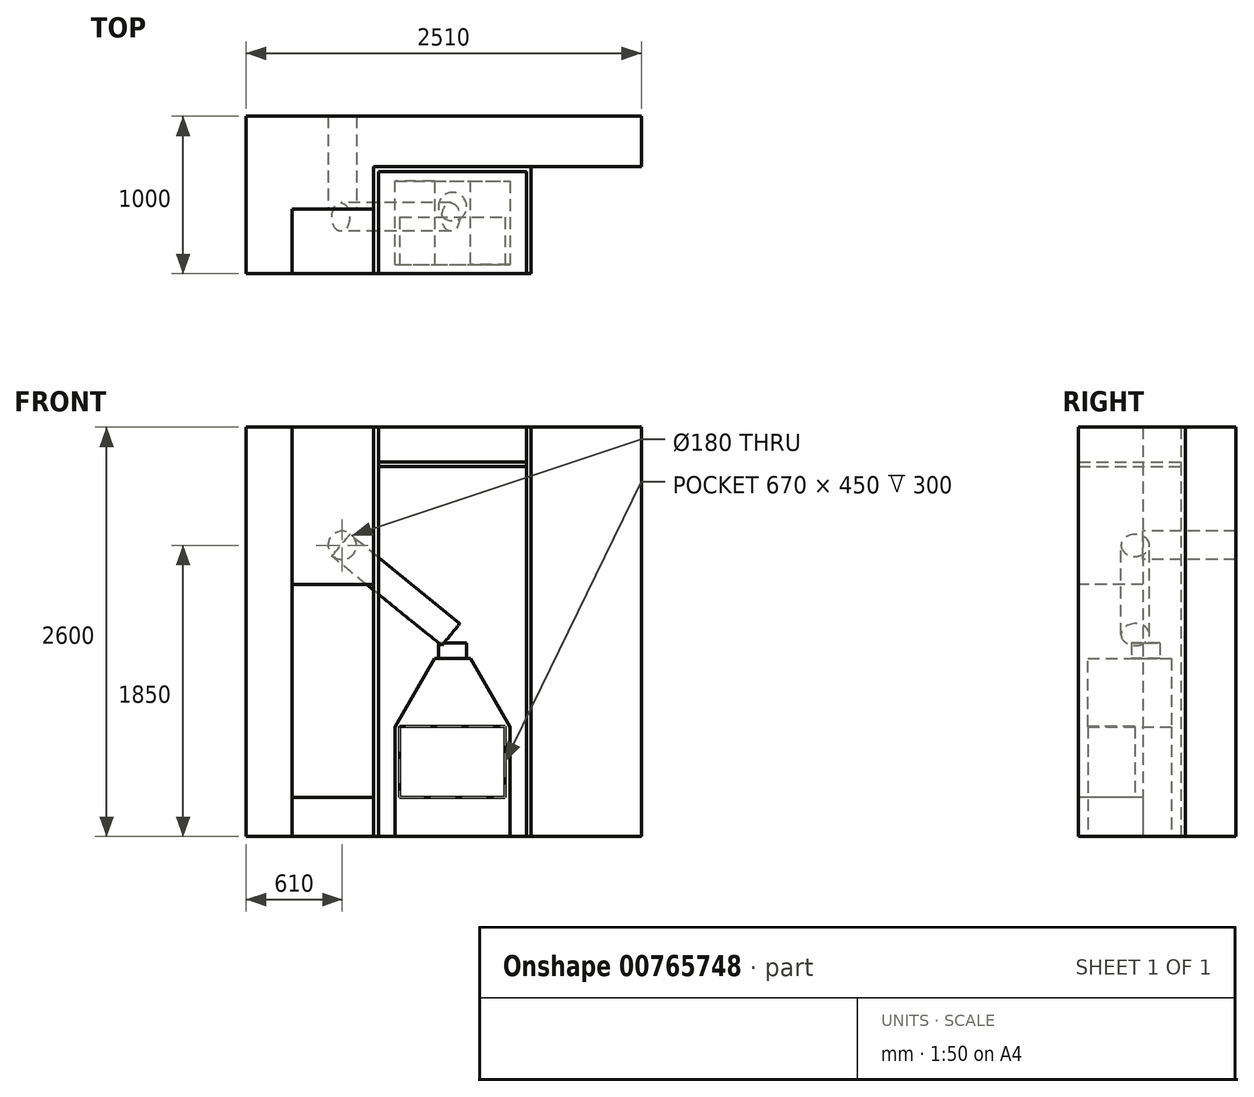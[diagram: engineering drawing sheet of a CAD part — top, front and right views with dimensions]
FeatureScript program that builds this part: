
annotation { "Feature Type Name" : "Feature", "Feature Type Description" : "" }
export const myFeature = defineFeature(function(context is Context, id is Id, definition is map)
    precondition{}
    {
        {
            var Q0;
            Q0=qCreatedBy(makeId("Top.planeOp"),FACE);
            var sketch = newSketch(context, id + "F0", { "sketchPlane" : qUnion([Q0])});
            skLineSegment(sketch, "E0", {"start": v(0, 0) * mm, "end": v(290, 0) * mm});
            skLineSegment(sketch, "E1", {"start": v(290, 0) * mm, "end": v(290, 410) * mm});
            skLineSegment(sketch, "E2", {"start": v(290, 410) * mm, "end": v(810, 410) * mm});
            skLineSegment(sketch, "E3", {"start": v(810, 410) * mm, "end": v(810, 680) * mm});
            skLineSegment(sketch, "E4", {"start": v(810, 680) * mm, "end": v(2510, 680) * mm});
            skLineSegment(sketch, "E5", {"start": v(2510, 680) * mm, "end": v(2510, 1000) * mm});
            skLineSegment(sketch, "E6", {"start": v(2510, 1000) * mm, "end": v(0, 1000) * mm});
            skLineSegment(sketch, "E7", {"start": v(0, 1000) * mm, "end": v(0, 0) * mm});
            skSolve(sketch);
        }
        {
            var Q0;
            Q0 = qSketchRegion(id + "F0", true);
            extrude(context, id + "F1", {"entities" : qUnion([Q0]), "depth" : 2600 * mm, "offsetDistance" : 25 * mm});
        }
        {
            var Q0;
            Q0=makeQuery(id+"F1.opExtrude","SWEPT_FACE",FACE,{"disambiguationData":[OSD([sQuery(id+"F0.wireOp",EDGE,"E2")])]});
            var sketch = newSketch(context, id + "F2", { "sketchPlane" : qUnion([Q0])});
            skCircle(sketch, "E8", {"center": v(610, 1850) * mm, "radius": 90 * mm});
            skSolve(sketch);
        }
        {
            var Q0;
            Q0 = qSketchRegion(id + "F2", true);
            extrude(context, id + "F3", {"entities" : qUnion([Q0]), "operationType" : NewBodyOperationType.REMOVE, "endBound" : BoundingType.THROUGH_ALL, "oppositeDirection" : true, "depth" : 25 * mm, "offsetDistance" : 25 * mm});
        }
        {
            var Q0;
            Q0=makeQuery(id+"F1.opExtrude","CAP_FACE",FACE,{"disambiguationData":[OSD([sQuery(id+"F0.wireOp",EDGE,"E0"),sQuery(id+"F0.wireOp",EDGE,"E1"),sQuery(id+"F0.wireOp",EDGE,"E2"),sQuery(id+"F0.wireOp",EDGE,"E3"),sQuery(id+"F0.wireOp",EDGE,"E4"),sQuery(id+"F0.wireOp",EDGE,"E5"),sQuery(id+"F0.wireOp",EDGE,"E6"),sQuery(id+"F0.wireOp",EDGE,"E7")])],"isStart":true});
            var sketch = newSketch(context, id + "F4", { "sketchPlane" : qUnion([Q0])});
            skLineSegment(sketch, "E9", {"start": v(810, -680) * mm, "end": v(810, 0) * mm});
            skLineSegment(sketch, "E10", {"start": v(810, 0) * mm, "end": v(840, 0) * mm});
            skLineSegment(sketch, "E11", {"start": v(840, 0) * mm, "end": v(840, -650) * mm});
            skLineSegment(sketch, "E12", {"start": v(840, -650) * mm, "end": v(1780, -650) * mm});
            skLineSegment(sketch, "E13", {"start": v(1780, -650) * mm, "end": v(1780, 0) * mm});
            skLineSegment(sketch, "E14", {"start": v(1780, 0) * mm, "end": v(1810, 0) * mm});
            skLineSegment(sketch, "E15", {"start": v(1810, 0) * mm, "end": v(1810, -680) * mm});
            skLineSegment(sketch, "E16", {"start": v(1810, -680) * mm, "end": v(810, -680) * mm});
            skSolve(sketch);
        }
        {
            var Q0;
            {var subQ0=sQuery(id+"F4.wireOp",EDGE,"E16");Q0=makeQuery(id+"F4.imprint","IMPRINT",FACE,{"disambiguationData":[TD([[makeQuery(id+"F4.imprint","IMPRINT",EDGE,{"derivedFrom":subQ0}),-1.0]])]});}
            var sketch = newSketch(context, id + "F5", { "sketchPlane" : qUnion([Q0])});
            skLineSegment(sketch, "E17.bottom", {"start": v(945, -588.8) * mm, "end": v(1675, -588.8) * mm});
            skLineSegment(sketch, "E17.top", {"start": v(945, -58.8) * mm, "end": v(1675, -58.8) * mm});
            skLineSegment(sketch, "E17.left", {"start": v(945, -588.8) * mm, "end": v(945, -58.8) * mm});
            skLineSegment(sketch, "E17.right", {"start": v(1675, -588.8) * mm, "end": v(1675, -58.8) * mm});
            skLineSegment(sketch, "E18", {"start": v(1310, -588.8) * mm, "end": v(1310, -58.8) * mm, "construction": true});
            skSolve(sketch);
        }
        {
            var Q0;
            Q0 = qSketchRegion(id + "F5", true);
            extrude(context, id + "F6", {"entities" : qUnion([Q0]), "oppositeDirection" : true, "depth" : 1130 * mm, "offsetDistance" : 25 * mm});
        }
        {
            var Q0;
            Q0=makeQuery(id+"F6.opExtrude","SWEPT_FACE",FACE,{"disambiguationData":[OSD([sQuery(id+"F5.wireOp",EDGE,"E17.top")])]});
            var sketch = newSketch(context, id + "F7", { "sketchPlane" : qUnion([Q0])});
            skLineSegment(sketch, "E19.bottom", {"start": v(975, 700) * mm, "end": v(1645, 700) * mm});
            skLineSegment(sketch, "E19.top", {"start": v(975, 250) * mm, "end": v(1645, 250) * mm});
            skLineSegment(sketch, "E19.left", {"start": v(975, 700) * mm, "end": v(975, 250) * mm});
            skLineSegment(sketch, "E19.right", {"start": v(1645, 700) * mm, "end": v(1645, 250) * mm});
            skLineSegment(sketch, "E20", {"start": v(1310, 700) * mm, "end": v(1310, 250) * mm, "construction": true});
            skSolve(sketch);
        }
        {
            var Q0;
            Q0 = qSketchRegion(id + "F7", true);
            extrude(context, id + "F8", {"entities" : qUnion([Q0]), "operationType" : NewBodyOperationType.REMOVE, "oppositeDirection" : true, "depth" : 300 * mm, "offsetDistance" : 25 * mm});
        }
        {
            var Q0;
            Q0=makeQuery(id+"F6.opExtrude","CAP_EDGE",EDGE,{"disambiguationData":[OSD([sQuery(id+"F5.wireOp",EDGE,"E17.left")])],"isStart":false});
            var Q1;
            Q1=makeQuery(id+"F6.opExtrude","CAP_EDGE",EDGE,{"disambiguationData":[OSD([sQuery(id+"F5.wireOp",EDGE,"E17.right")])],"isStart":false});
            chamfer(context, id + "F9", {"entities" : qUnion([Q0, Q1]), "chamferType" : ChamferType.OFFSET_ANGLE, "width" : 250 * mm, "oppositeDirection" : false, "angle" : 60 * degree, "tangentPropagation" : true});
        }
        {
            var Q0;
            Q0=makeQuery(id+"F6.opExtrude","CAP_FACE",FACE,{"disambiguationData":[OSD([sQuery(id+"F5.wireOp",EDGE,"E17.bottom"),sQuery(id+"F5.wireOp",EDGE,"E17.top"),sQuery(id+"F5.wireOp",EDGE,"E17.left"),sQuery(id+"F5.wireOp",EDGE,"E17.right")])],"isStart":false});
            var sketch = newSketch(context, id + "F10", { "sketchPlane" : qUnion([Q0])});
            skLineSegment(sketch, "E21", {"start": v(1310, 588.8) * mm, "end": v(1310, 58.8) * mm, "construction": true});
            skCircle(sketch, "E22", {"center": v(1310, 426.38) * mm, "radius": 90 * mm});
            skSolve(sketch);
        }
        {
            var Q0;
            Q0 = qSketchRegion(id + "F10", true);
            extrude(context, id + "F11", {"entities" : qUnion([Q0]), "operationType" : NewBodyOperationType.ADD, "depth" : 100 * mm, "offsetDistance" : 25 * mm});
        }
        {
            var Q0;
            Q0=makeQuery(id+"F6.opExtrude","SWEPT_FACE",FACE,{"disambiguationData":[OSD([sQuery(id+"F5.wireOp",EDGE,"E17.top")])]});
            cPlane(context, id + "F12", {"entities" : qUnion([Q0]), "cplaneType" : CPlaneType.OFFSET, "offset" : 250 * mm, "oppositeDirection" : true, "width" : 150 * mm, "height" : 150 * mm});
        }
        {
            var Q0;
            Q0=qCreatedBy(id+"F12.planeOp",FACE);
            var sketch = newSketch(context, id + "F13", { "sketchPlane" : qUnion([Q0])});
            skLineSegment(sketch, "E23", {"start": v(602.67, 1852.05) * mm, "end": v(1285.65, 1297.5) * mm});
            skSolve(sketch);
        }
        {
            var Q0;
            Q0=sQuery(id+"F13.wireOp",VERTEX,"E23.start");
            var Q1;
            Q1=sQuery(id+"F13.wireOp",EDGE,"E23");
            cPlane(context, id + "F14", {"entities" : qUnion([Q0, Q1]), "cplaneType" : CPlaneType.LINE_POINT, "offset" : 25 * mm, "width" : 150 * mm, "height" : 150 * mm});
        }
        {
            var Q0;
            Q0=qCreatedBy(id+"F14.planeOp",FACE);
            var sketch = newSketch(context, id + "F15", { "sketchPlane" : qUnion([Q0])});
            skCircle(sketch, "E24", {"center": v(360.62, 1814.99) * mm, "radius": 90 * mm});
            skSolve(sketch);
        }
        {
            var Q0;
            Q0 = qSketchRegion(id + "F15", true);
            extrude(context, id + "F16", {"entities" : qUnion([Q0]), "depth" : 900 * mm, "offsetDistance" : 25 * mm});
        }
        {
            var Q0;
            {var subQ0=sQuery(id+"F4.wireOp",EDGE,"E16");Q0=makeQuery(id+"F4.imprint","IMPRINT",FACE,{"disambiguationData":[TD([[makeQuery(id+"F4.imprint","IMPRINT",EDGE,{"derivedFrom":subQ0}),-1.0]])]});}
            var sketch = newSketch(context, id + "F17", { "sketchPlane" : qUnion([Q0])});
            skLineSegment(sketch, "E25.0", {"start": v(290, 0) * mm, "end": v(290, -410) * mm});
            skLineSegment(sketch, "E26.0", {"start": v(290, -410) * mm, "end": v(810, -410) * mm});
            skLineSegment(sketch, "E27", {"start": v(810, -410) * mm, "end": v(810, 0) * mm});
            skLineSegment(sketch, "E28", {"start": v(810, 0) * mm, "end": v(290, 0) * mm});
            skSolve(sketch);
        }
        {
            var Q0;
            Q0 = qSketchRegion(id + "F17", true);
            extrude(context, id + "F18", {"entities" : qUnion([Q0]), "oppositeDirection" : true, "depth" : 250 * mm, "offsetDistance" : 25 * mm});
        }
        {
            var Q0;
            Q0 = qSketchRegion(id + "F17", true);
            var Q1;
            Q1=makeQuery(id+"F1.opExtrude","CAP_FACE",FACE,{"disambiguationData":[OSD([sQuery(id+"F0.wireOp",EDGE,"E0"),sQuery(id+"F0.wireOp",EDGE,"E1"),sQuery(id+"F0.wireOp",EDGE,"E2"),sQuery(id+"F0.wireOp",EDGE,"E3"),sQuery(id+"F0.wireOp",EDGE,"E4"),sQuery(id+"F0.wireOp",EDGE,"E5"),sQuery(id+"F0.wireOp",EDGE,"E6"),sQuery(id+"F0.wireOp",EDGE,"E7")])],"isStart":false});
            extrude(context, id + "F19", {"entities" : qUnion([Q0]), "endBound" : BoundingType.UP_TO_SURFACE, "oppositeDirection" : true, "depth" : 2370 * mm, "endBoundEntityFace" : qUnion([Q1]), "offsetDistance" : 25 * mm, "hasSecondDirection" : true, "secondDirectionOppositeDirection" : true, "secondDirectionDepth" : 1600 * mm});
        }
        {
            var Q0;
            Q0 = qSketchRegion(id + "F4", true);
            var Q1;
            Q1=makeQuery(id+"F1.opExtrude","CAP_FACE",FACE,{"disambiguationData":[OSD([sQuery(id+"F0.wireOp",EDGE,"E0"),sQuery(id+"F0.wireOp",EDGE,"E1"),sQuery(id+"F0.wireOp",EDGE,"E2"),sQuery(id+"F0.wireOp",EDGE,"E3"),sQuery(id+"F0.wireOp",EDGE,"E4"),sQuery(id+"F0.wireOp",EDGE,"E5"),sQuery(id+"F0.wireOp",EDGE,"E6"),sQuery(id+"F0.wireOp",EDGE,"E7")])],"isStart":false});
            extrude(context, id + "F20", {"entities" : qUnion([Q0]), "endBound" : BoundingType.UP_TO_SURFACE, "oppositeDirection" : true, "depth" : 25 * mm, "endBoundEntityFace" : qUnion([Q1]), "offsetDistance" : 25 * mm});
        }
        {
            var Q0;
            Q0=makeQuery(id+"F20.opExtrude","CAP_FACE",FACE,{"disambiguationData":[OSD([sQuery(id+"F4.wireOp",EDGE,"E9"),sQuery(id+"F4.wireOp",EDGE,"E10"),sQuery(id+"F4.wireOp",EDGE,"E11"),sQuery(id+"F4.wireOp",EDGE,"E12"),sQuery(id+"F4.wireOp",EDGE,"E13"),sQuery(id+"F4.wireOp",EDGE,"E14"),sQuery(id+"F4.wireOp",EDGE,"E15"),sQuery(id+"F4.wireOp",EDGE,"E16")])],"isStart":false});
            cPlane(context, id + "F21", {"entities" : qUnion([Q0]), "cplaneType" : CPlaneType.OFFSET, "offset" : 250 * mm, "oppositeDirection" : true, "width" : 150 * mm, "height" : 150 * mm});
        }
        {
            var Q0;
            Q0=qCreatedBy(id+"F21.planeOp",FACE);
            var sketch = newSketch(context, id + "F22", { "sketchPlane" : qUnion([Q0])});
            skLineSegment(sketch, "E29.0", {"start": v(840, 0) * mm, "end": v(840, 650) * mm});
            skLineSegment(sketch, "E30.0.0", {"start": v(1780, 650) * mm, "end": v(840, 650) * mm});
            skLineSegment(sketch, "E30.0.2", {"start": v(840, 650) * mm, "end": v(1780, 650) * mm});
            skLineSegment(sketch, "E31.0", {"start": v(1780, 650) * mm, "end": v(1780, 0) * mm});
            skLineSegment(sketch, "E32", {"start": v(840, 0) * mm, "end": v(1780, 0) * mm});
            skSolve(sketch);
        }
        {
            var Q0;
            Q0 = qSketchRegion(id + "F22", true);
            extrude(context, id + "F23", {"entities" : qUnion([Q0]), "depth" : 30 * mm, "offsetDistance" : 25 * mm});
        }
    });
